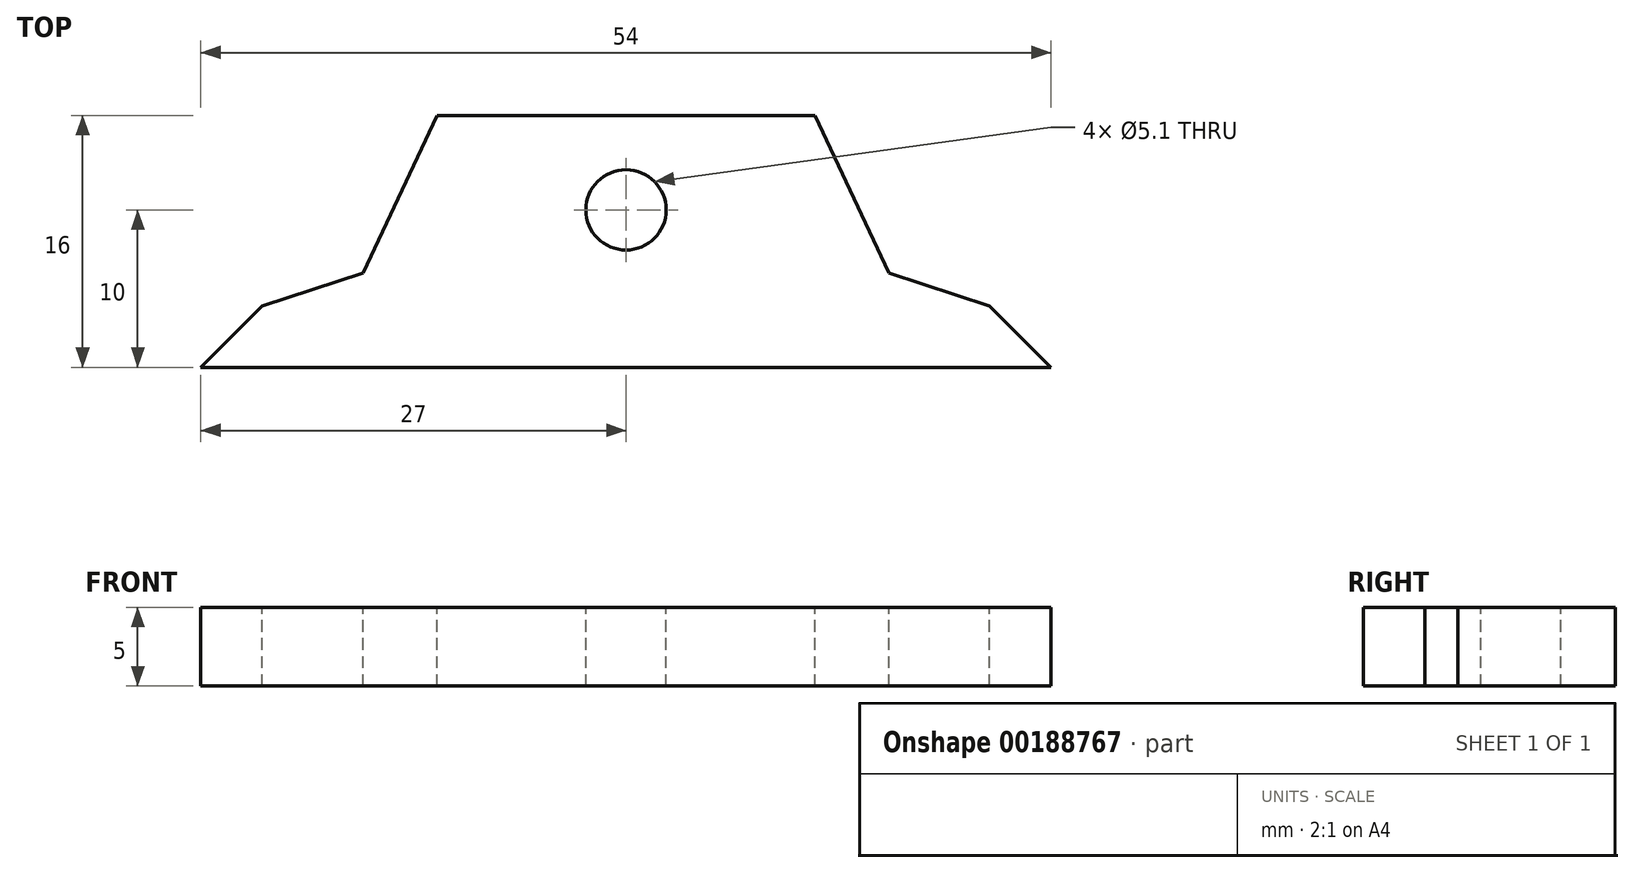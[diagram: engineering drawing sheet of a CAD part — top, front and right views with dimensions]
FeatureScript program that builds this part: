
annotation { "Feature Type Name" : "Feature", "Feature Type Description" : "" }
export const myFeature = defineFeature(function(context is Context, id is Id, definition is map)
    precondition{}
    {
        {
            var Q0;
            Q0=qCreatedBy(makeId("Top.planeOp"),FACE);
            var sketch = newSketch(context, id + "F0", { "sketchPlane" : qUnion([Q0])});
            skLineSegment(sketch, "E0.bottom", {"start": v(35, -17) * mm, "end": v(-35, -17) * mm});
            skLineSegment(sketch, "E0.top", {"start": v(35, 17) * mm, "end": v(-35, 17) * mm});
            skLineSegment(sketch, "E0.left", {"start": v(35, -17) * mm, "end": v(35, 17) * mm});
            skLineSegment(sketch, "E0.right", {"start": v(-35, -17) * mm, "end": v(-35, 17) * mm});
            skPoint(sketch, "E0.middle", {"position": v(0, 0) * mm});
            skLineSegment(sketch, "E1", {"start": v(-12, 33) * mm, "end": v(12, 33) * mm});
            skLineSegment(sketch, "E2", {"start": v(0, -17) * mm, "end": v(0, 33) * mm, "construction": true});
            skLineSegment(sketch, "E3", {"start": v(23, -17) * mm, "end": v(23, 17) * mm, "construction": true});
            skLineSegment(sketch, "E4", {"start": v(-23, -17) * mm, "end": v(-23, 17) * mm, "construction": true});
            skLineSegment(sketch, "E5", {"start": v(-35, -12) * mm, "end": v(35, -12) * mm, "construction": true});
            skLineSegment(sketch, "E6", {"start": v(-35, 12) * mm, "end": v(35, 12) * mm, "construction": true});
            skCircle(sketch, "E7", {"center": v(23, 12) * mm, "radius": 1.5 * mm});
            skCircle(sketch, "E8", {"center": v(23, -12) * mm, "radius": 1.5 * mm});
            skCircle(sketch, "E9", {"center": v(-23, -12) * mm, "radius": 1.5 * mm});
            skCircle(sketch, "E10", {"center": v(-23, 12) * mm, "radius": 1.5 * mm});
            skCircle(sketch, "E11", {"center": v(0, 27) * mm, "radius": 2.55 * mm});
            skCircle(sketch, "E12", {"center": v(0, -6) * mm, "radius": 2.55 * mm});
            skCircle(sketch, "E13", {"center": v(28, 3.9) * mm, "radius": 2.25 * mm});
            skCircle(sketch, "E14", {"center": v(-28, 3.9) * mm, "radius": 2.25 * mm});
            skLineSegment(sketch, "E15", {"start": v(-12, 33) * mm, "end": v(-16.7, 23) * mm});
            skLineSegment(sketch, "E16", {"start": v(-16.7, 23) * mm, "end": v(-35, 17) * mm});
            skLineSegment(sketch, "E17", {"start": v(12, 33) * mm, "end": v(16.7, 23) * mm});
            skLineSegment(sketch, "E18", {"start": v(16.7, 23) * mm, "end": v(35, 17) * mm});
            skLineSegment(sketch, "E19", {"start": v(35, -9) * mm, "end": v(27, -17) * mm});
            skLineSegment(sketch, "E20", {"start": v(-27, -17) * mm, "end": v(-35, -9) * mm});
            skLineSegment(sketch, "E21", {"start": v(35, -17) * mm, "end": v(27, -17) * mm});
            skLineSegment(sketch, "E22", {"start": v(35, 9) * mm, "end": v(23.1, 20.9) * mm});
            skLineSegment(sketch, "E23", {"start": v(-35, 9) * mm, "end": v(-23.1, 20.9) * mm});
            skSolve(sketch);
        }
        {
            var Q0;
            Q0=makeQuery(id+"F0.imprint","IMPRINT",FACE,{"disambiguationData":[TD([[makeQuery(id+"F0.imprint","IMPRINT",EDGE,{"derivedFrom":sQuery(id+"F0.wireOp",EDGE,"E1")}),-1.0]])]});
            var Q1;
            Q1=makeQuery(id+"F0.imprint","IMPRINT",FACE,{"disambiguationData":[TD([[makeQuery(id+"F0.imprint","IMPRINT",EDGE,{"derivedFrom":sQuery(id+"F0.wireOp",EDGE,"E7")}),-1.0]])]});
            extrude(context, id + "F1", {"entities" : qUnion([Q0, Q1]), "oppositeDirection" : true, "depth" : 5 * mm, "offsetDistance" : 25 * mm});
        }
    });
